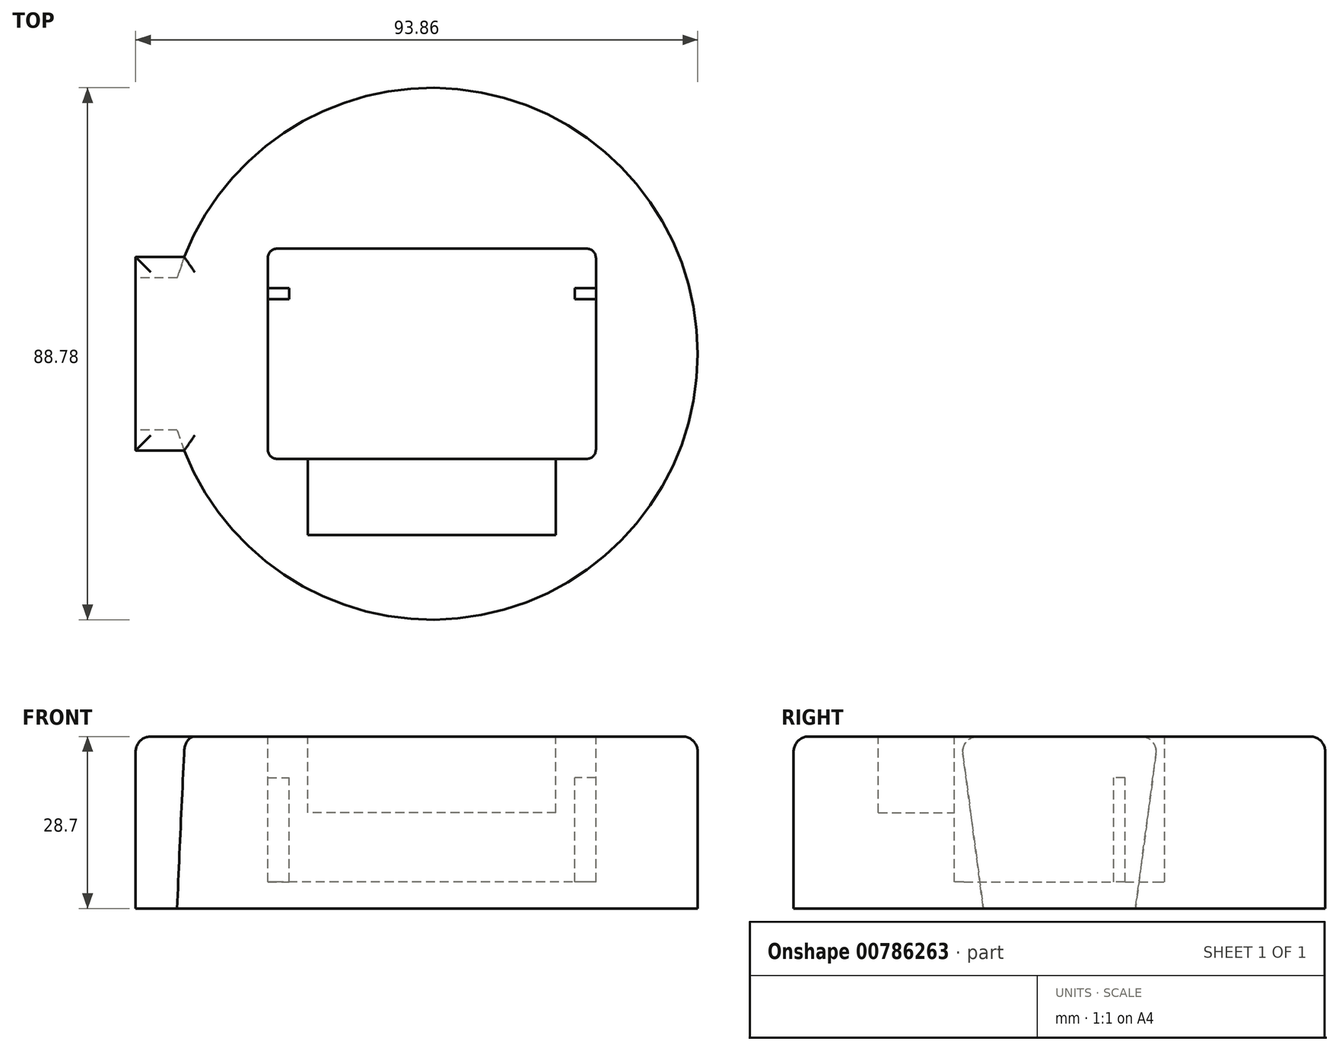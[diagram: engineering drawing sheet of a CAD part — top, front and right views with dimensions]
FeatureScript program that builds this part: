
annotation { "Feature Type Name" : "Feature", "Feature Type Description" : "" }
export const myFeature = defineFeature(function(context is Context, id is Id, definition is map)
    precondition{}
    {
        {
            var Q0;
            Q0=qCreatedBy(makeId("Top.planeOp"),FACE);
            var sketch = newSketch(context, id + "F0", { "sketchPlane" : qUnion([Q0])});
            skCircle(sketch, "E0", {"center": v(0, 0) * mm, "radius": 44.39 * mm});
            skSolve(sketch);
        }
        {
            var Q0;
            Q0 = qSketchRegion(id + "F0", true);
            extrude(context, id + "F1", {"entities" : qUnion([Q0]), "oppositeDirection" : true, "depth" : 28.7 * mm, "offsetDistance" : 25.4 * mm});
        }
        {
            var Q0;
            Q0=makeQuery(id+"F1.opExtrude","CAP_FACE",FACE,{"disambiguationData":[OSD([sQuery(id+"F0.wireOp",EDGE,"E0")])],"isStart":false});
            var sketch = newSketch(context, id + "F2", { "sketchPlane" : qUnion([Q0])});
            skCircle(sketch, "E1", {"center": v(0, 0) * mm, "radius": 35.94 * mm});
            skSolve(sketch);
        }
        {
            var Q0;
            Q0 = qSketchRegion(id + "F2", true);
            extrude(context, id + "F3", {"entities" : qUnion([Q0]), "operationType" : NewBodyOperationType.ADD, "depth" : 21.08 * mm, "offsetDistance" : 25.4 * mm});
        }
        {
            var Q0;
            Q0=makeQuery(id+"F1.opExtrude","CAP_FACE",FACE,{"disambiguationData":[OSD([sQuery(id+"F0.wireOp",EDGE,"E0")])],"isStart":true});
            var sketch = newSketch(context, id + "F4", { "sketchPlane" : qUnion([Q0])});
            skLineSegment(sketch, "E2.bottom", {"start": v(0, 16.51) * mm, "end": v(-49.47, 16.51) * mm});
            skLineSegment(sketch, "E2.top", {"start": v(0, -16.51) * mm, "end": v(-49.47, -16.51) * mm});
            skLineSegment(sketch, "E2.left", {"start": v(0, 16.51) * mm, "end": v(0, -16.51) * mm});
            skLineSegment(sketch, "E2.right", {"start": v(-49.47, 16.5) * mm, "end": v(-49.47, -16.51) * mm});
            skPoint(sketch, "E3", {"position": v(0, 0) * mm});
            skPoint(sketch, "E4.visualSharp", {"position": v(-49.47, 16.51) * mm});
            skPoint(sketch, "E5.visualSharp", {"position": v(-49.47, -16.51) * mm});
            skSolve(sketch);
        }
        {
            var Q0;
            Q0 = qSketchRegion(id + "F4", true);
            var Q1;
            Q1=makeQuery(id+"F1.opExtrude","CAP_FACE",FACE,{"disambiguationData":[OSD([sQuery(id+"F0.wireOp",EDGE,"E0")])],"isStart":false});
            extrude(context, id + "F5", {"entities" : qUnion([Q0]), "operationType" : NewBodyOperationType.ADD, "endBound" : BoundingType.UP_TO_SURFACE, "oppositeDirection" : true, "depth" : 25.4 * mm, "endBoundEntityFace" : qUnion([Q1]), "offsetDistance" : 25.4 * mm});
        }
        {
            var Q0;
            Q0=makeQuery(id+"F5.boolean.opBoolean","MERGE",FACE,{"derivedFrom":[makeQuery(id+"F1.opExtrude","CAP_FACE",FACE,{"disambiguationData":[OSD([sQuery(id+"F0.wireOp",EDGE,"E0")])],"isStart":true}),makeQuery(id+"F5.opExtrude","CAP_FACE",FACE,{"disambiguationData":[OSD([sQuery(id+"F4.wireOp",EDGE,"E2.bottom"),sQuery(id+"F4.wireOp",EDGE,"E2.top"),sQuery(id+"F4.wireOp",EDGE,"E2.left"),sQuery(id+"F4.wireOp",EDGE,"E2.right")])],"isStart":true})]});
            var sketch = newSketch(context, id + "F6", { "sketchPlane" : qUnion([Q0])});
            skLineSegment(sketch, "E6.bottom", {"start": v(25.8, -17.55) * mm, "end": v(-25.8, -17.55) * mm});
            skLineSegment(sketch, "E6.top", {"start": v(25.8, 17.55) * mm, "end": v(-25.8, 17.55) * mm});
            skLineSegment(sketch, "E6.left", {"start": v(27.4, -15.96) * mm, "end": v(27.4, 15.96) * mm});
            skLineSegment(sketch, "E6.right", {"start": v(-27.4, -15.96) * mm, "end": v(-27.4, 15.96) * mm});
            skPoint(sketch, "E6.middle", {"position": v(0, 0) * mm});
            skPoint(sketch, "E7.visualSharp", {"position": v(-27.4, 17.55) * mm});
            skArc(sketch, "E7.filletArc", {"start": v(-25.8, 17.55) * mm, "mid": v(-26.93, 17.09) * mm, "end": v(-27.4, 15.96) * mm});
            skPoint(sketch, "E8.visualSharp", {"position": v(-27.4, -17.55) * mm});
            skArc(sketch, "E8.filletArc", {"start": v(-27.4, -15.96) * mm, "mid": v(-26.93, -17.09) * mm, "end": v(-25.8, -17.55) * mm});
            skPoint(sketch, "E9.visualSharp", {"position": v(27.4, -17.55) * mm});
            skArc(sketch, "E9.filletArc", {"start": v(25.8, -17.55) * mm, "mid": v(26.93, -17.09) * mm, "end": v(27.4, -15.96) * mm});
            skPoint(sketch, "E10.visualSharp", {"position": v(27.4, 17.55) * mm});
            skArc(sketch, "E10.filletArc", {"start": v(27.4, 15.96) * mm, "mid": v(26.93, 17.09) * mm, "end": v(25.8, 17.55) * mm});
            skSolve(sketch);
        }
        {
            var Q0;
            Q0 = qSketchRegion(id + "F6", true);
            extrude(context, id + "F7", {"entities" : qUnion([Q0]), "operationType" : NewBodyOperationType.REMOVE, "oppositeDirection" : true, "depth" : 24.28 * mm, "offsetDistance" : 25.4 * mm});
        }
        {
            var Q0;
            Q0=qCreatedBy(makeId("Top.planeOp"),FACE);
            var sketch = newSketch(context, id + "F8", { "sketchPlane" : qUnion([Q0])});
            skLineSegment(sketch, "E11.bottom", {"start": v(-23.84, 9.1) * mm, "end": v(-27.4, 9.1) * mm});
            skLineSegment(sketch, "E11.top", {"start": v(-23.84, 10.95) * mm, "end": v(-27.4, 10.95) * mm});
            skLineSegment(sketch, "E11.left", {"start": v(-23.84, 9.1) * mm, "end": v(-23.84, 10.95) * mm});
            skLineSegment(sketch, "E11.right", {"start": v(-27.4, 9.1) * mm, "end": v(-27.4, 10.95) * mm});
            skPoint(sketch, "E11.middle", {"position": v(-25.62, 10.02) * mm});
            skLineSegment(sketch, "E12.bottom", {"start": v(23.84, 10.95) * mm, "end": v(27.4, 10.95) * mm});
            skLineSegment(sketch, "E12.top", {"start": v(23.84, 9.1) * mm, "end": v(27.4, 9.1) * mm});
            skLineSegment(sketch, "E12.left", {"start": v(23.84, 10.95) * mm, "end": v(23.84, 9.1) * mm});
            skLineSegment(sketch, "E12.right", {"start": v(27.4, 10.95) * mm, "end": v(27.4, 9.1) * mm});
            skPoint(sketch, "E12.middle", {"position": v(25.62, 10.02) * mm});
            skSolve(sketch);
        }
        {
            var Q0;
            Q0 = qSketchRegion(id + "F8", true);
            var Q1;
            Q1=makeQuery(id+"F7.boolean.opBoolean","COPY",FACE,{"derivedFrom":makeQuery(id+"F7.opExtrude","CAP_FACE",FACE,{"disambiguationData":[OSD([sQuery(id+"F6.wireOp",EDGE,"E6.bottom"),sQuery(id+"F6.wireOp",EDGE,"E6.top"),sQuery(id+"F6.wireOp",EDGE,"E6.left"),sQuery(id+"F6.wireOp",EDGE,"E6.right"),sQuery(id+"F6.wireOp",EDGE,"E7.filletArc"),sQuery(id+"F6.wireOp",EDGE,"E8.filletArc"),sQuery(id+"F6.wireOp",EDGE,"E9.filletArc"),sQuery(id+"F6.wireOp",EDGE,"E10.filletArc")])],"isStart":false})});
            extrude(context, id + "F9", {"entities" : qUnion([Q0]), "operationType" : NewBodyOperationType.ADD, "endBound" : BoundingType.UP_TO_SURFACE, "oppositeDirection" : true, "depth" : 25.4 * mm, "endBoundEntityFace" : qUnion([Q1]), "offsetDistance" : 25.4 * mm});
        }
        {
            var Q0;
            Q0=makeQuery(id+"F9.boolean.opBoolean","MERGE",FACE,{"derivedFrom":[makeQuery(id+"F5.boolean.opBoolean","MERGE",FACE,{"derivedFrom":[makeQuery(id+"F1.opExtrude","CAP_FACE",FACE,{"disambiguationData":[OSD([sQuery(id+"F0.wireOp",EDGE,"E0")])],"isStart":true}),makeQuery(id+"F5.opExtrude","CAP_FACE",FACE,{"disambiguationData":[OSD([sQuery(id+"F4.wireOp",EDGE,"E2.bottom"),sQuery(id+"F4.wireOp",EDGE,"E2.top"),sQuery(id+"F4.wireOp",EDGE,"E2.left"),sQuery(id+"F4.wireOp",EDGE,"E2.right")])],"isStart":true})]}),makeQuery(id+"F9.opExtrude","CAP_FACE",FACE,{"disambiguationData":[OSD([sQuery(id+"F8.wireOp",EDGE,"E11.bottom"),sQuery(id+"F8.wireOp",EDGE,"E11.top"),sQuery(id+"F8.wireOp",EDGE,"E11.left"),sQuery(id+"F8.wireOp",EDGE,"E11.right")])],"isStart":true}),makeQuery(id+"F9.opExtrude","CAP_FACE",FACE,{"disambiguationData":[OSD([sQuery(id+"F8.wireOp",EDGE,"E12.bottom"),sQuery(id+"F8.wireOp",EDGE,"E12.top"),sQuery(id+"F8.wireOp",EDGE,"E12.left"),sQuery(id+"F8.wireOp",EDGE,"E12.right")])],"isStart":true})]});
            var sketch = newSketch(context, id + "F10", { "sketchPlane" : qUnion([Q0])});
            skLineSegment(sketch, "E13.bottom", {"start": v(-27.4, 13.46) * mm, "end": v(27.4, 13.46) * mm});
            skLineSegment(sketch, "E13.top", {"start": v(-27.4, 5.6) * mm, "end": v(27.4, 5.6) * mm});
            skLineSegment(sketch, "E13.left", {"start": v(-27.4, 13.46) * mm, "end": v(-27.4, 5.6) * mm});
            skLineSegment(sketch, "E13.right", {"start": v(27.4, 13.46) * mm, "end": v(27.4, 5.6) * mm});
            skSolve(sketch);
        }
        {
            var Q0;
            Q0 = qSketchRegion(id + "F10", true);
            extrude(context, id + "F11", {"entities" : qUnion([Q0]), "operationType" : NewBodyOperationType.REMOVE, "oppositeDirection" : true, "depth" : 6.86 * mm, "offsetDistance" : 25.4 * mm});
        }
        {
            var Q0;
            Q0=makeQuery(id+"F9.boolean.opBoolean","MERGE",FACE,{"derivedFrom":[makeQuery(id+"F5.boolean.opBoolean","MERGE",FACE,{"derivedFrom":[makeQuery(id+"F1.opExtrude","CAP_FACE",FACE,{"disambiguationData":[OSD([sQuery(id+"F0.wireOp",EDGE,"E0")])],"isStart":true}),makeQuery(id+"F5.opExtrude","CAP_FACE",FACE,{"disambiguationData":[OSD([sQuery(id+"F4.wireOp",EDGE,"E2.bottom"),sQuery(id+"F4.wireOp",EDGE,"E2.top"),sQuery(id+"F4.wireOp",EDGE,"E2.left"),sQuery(id+"F4.wireOp",EDGE,"E2.right")])],"isStart":true})]}),makeQuery(id+"F9.opExtrude","CAP_FACE",FACE,{"disambiguationData":[OSD([sQuery(id+"F8.wireOp",EDGE,"E11.bottom"),sQuery(id+"F8.wireOp",EDGE,"E11.top"),sQuery(id+"F8.wireOp",EDGE,"E11.left"),sQuery(id+"F8.wireOp",EDGE,"E11.right")])],"isStart":true}),makeQuery(id+"F9.opExtrude","CAP_FACE",FACE,{"disambiguationData":[OSD([sQuery(id+"F8.wireOp",EDGE,"E12.bottom"),sQuery(id+"F8.wireOp",EDGE,"E12.top"),sQuery(id+"F8.wireOp",EDGE,"E12.left"),sQuery(id+"F8.wireOp",EDGE,"E12.right")])],"isStart":true})]});
            var sketch = newSketch(context, id + "F12", { "sketchPlane" : qUnion([Q0])});
            skLineSegment(sketch, "E14.bottom", {"start": v(20.7, -30.25) * mm, "end": v(-20.7, -30.25) * mm});
            skLineSegment(sketch, "E14.top", {"start": v(20.7, -17.55) * mm, "end": v(-20.7, -17.55) * mm});
            skLineSegment(sketch, "E14.left", {"start": v(20.7, -30.25) * mm, "end": v(20.7, -17.55) * mm});
            skLineSegment(sketch, "E14.right", {"start": v(-20.7, -30.25) * mm, "end": v(-20.7, -17.55) * mm});
            skPoint(sketch, "E14.middle", {"position": v(0, -23.9) * mm});
            skSolve(sketch);
        }
        {
            var Q0;
            Q0 = qSketchRegion(id + "F12", true);
            extrude(context, id + "F13", {"entities" : qUnion([Q0]), "operationType" : NewBodyOperationType.REMOVE, "oppositeDirection" : true, "depth" : 12.7 * mm, "offsetDistance" : 25.4 * mm});
        }
        {
            var Q0;
            Q0=makeQuery(id+"F5.boolean.opBoolean","MERGE",FACE,{"derivedFrom":[makeQuery(id+"F1.opExtrude","CAP_FACE",FACE,{"disambiguationData":[OSD([sQuery(id+"F0.wireOp",EDGE,"E0")])],"isStart":false}),makeQuery(id+"F5.opExtrude","CAP_FACE",FACE,{"disambiguationData":[OSD([sQuery(id+"F4.wireOp",EDGE,"E2.bottom"),sQuery(id+"F4.wireOp",EDGE,"E2.top"),sQuery(id+"F4.wireOp",EDGE,"E2.left"),sQuery(id+"F4.wireOp",EDGE,"E2.right")])],"isStart":false})]});
            var sketch = newSketch(context, id + "F14", { "sketchPlane" : qUnion([Q0])});
            skCircle(sketch, "E15", {"center": v(0, 0) * mm, "radius": 38.1 * mm});
            skSolve(sketch);
        }
        {
            var Q0;
            Q0 = qSketchRegion(id + "F14", true);
            var Q1;
            Q1=makeQuery(id+"F3.opExtrude","CAP_FACE",FACE,{"disambiguationData":[OSD([sQuery(id+"F2.wireOp",EDGE,"E1")])],"isStart":false});
            extrude(context, id + "F15", {"entities" : qUnion([Q0]), "operationType" : NewBodyOperationType.REMOVE, "endBound" : BoundingType.UP_TO_SURFACE, "depth" : 25.4 * mm, "endBoundEntityFace" : qUnion([Q1]), "offsetDistance" : 25.4 * mm});
        }
        {
            var Q0;
            Q0=makeQuery(id+"F5.opExtrude","SWEPT_FACE",FACE,{"disambiguationData":[OSD([sQuery(id+"F4.wireOp",EDGE,"E2.right")])]});
            var sketch = newSketch(context, id + "F16", { "sketchPlane" : qUnion([Q0])});
            skLineSegment(sketch, "E16", {"start": v(16.51, 0) * mm, "end": v(12.7, -28.7) * mm});
            skLineSegment(sketch, "E17", {"start": v(-12.7, -28.7) * mm, "end": v(-16.51, 0) * mm});
            skLineSegment(sketch, "E18", {"start": v(-16.51, 0) * mm, "end": v(-16.51, -28.7) * mm});
            skLineSegment(sketch, "E19", {"start": v(-16.51, -28.7) * mm, "end": v(-12.7, -28.7) * mm});
            skLineSegment(sketch, "E20", {"start": v(16.51, 0) * mm, "end": v(16.51, -28.7) * mm});
            skLineSegment(sketch, "E21", {"start": v(16.51, -28.7) * mm, "end": v(12.7, -28.7) * mm});
            skSolve(sketch);
        }
        {
            var Q0;
            Q0 = qSketchRegion(id + "F16", true);
            var Q1;
            Q1=makeQuery(id+"F1.opExtrude","SWEPT_FACE",FACE,{"disambiguationData":[OSD([sQuery(id+"F0.wireOp",EDGE,"E0")])]});
            extrude(context, id + "F17", {"entities" : qUnion([Q0]), "operationType" : NewBodyOperationType.REMOVE, "endBound" : BoundingType.UP_TO_SURFACE, "oppositeDirection" : true, "depth" : 25.4 * mm, "endBoundEntityFace" : qUnion([Q1]), "offsetDistance" : 25.4 * mm});
        }
        {
            var Q0;
            Q0=makeQuery(id+"F1.opExtrude","CAP_EDGE",EDGE,{"disambiguationData":[OSD([sQuery(id+"F0.wireOp",EDGE,"E0")])],"isStart":true});
            var Q1;
            Q1=makeQuery(id+"F17.boolean.opBoolean","MERGE",EDGE,{"derivedFrom":[makeQuery(id+"F5.opExtrude","CAP_EDGE",EDGE,{"disambiguationData":[OSD([sQuery(id+"F4.wireOp",EDGE,"E2.top")])],"isStart":true})],"fromTools":[makeQuery(id+"F17.opExtrude","SWEPT_EDGE",EDGE,{"disambiguationData":[OSD([sQuery(id+"F4.wireOp",EDGE,"E2.right"),sQuery(id+"F16.wireOp",EDGE,"E16"),sQuery(id+"F16.wireOp",EDGE,"E20")])]})]});
            var Q2;
            Q2=makeQuery(id+"F17.boolean.opBoolean","COPY",EDGE,{"derivedFrom":makeQuery(id+"F17.opExtrude","CAP_EDGE",EDGE,{"disambiguationData":[OSD([sQuery(id+"F16.wireOp",EDGE,"E16")])],"isStart":true})});
            var Q3;
            Q3=makeQuery(id+"F5.opExtrude","CAP_EDGE",EDGE,{"disambiguationData":[OSD([sQuery(id+"F4.wireOp",EDGE,"E2.right")])],"isStart":true});
            var Q4;
            Q4=makeQuery(id+"F17.boolean.opBoolean","COPY",EDGE,{"derivedFrom":makeQuery(id+"F17.opExtrude","CAP_EDGE",EDGE,{"disambiguationData":[OSD([sQuery(id+"F16.wireOp",EDGE,"E17")])],"isStart":true})});
            var Q5;
            Q5=makeQuery(id+"F17.boolean.opBoolean","MERGE",EDGE,{"derivedFrom":[makeQuery(id+"F5.opExtrude","CAP_EDGE",EDGE,{"disambiguationData":[OSD([sQuery(id+"F4.wireOp",EDGE,"E2.bottom")])],"isStart":true})],"fromTools":[makeQuery(id+"F17.opExtrude","SWEPT_EDGE",EDGE,{"disambiguationData":[OSD([sQuery(id+"F4.wireOp",EDGE,"E2.right"),sQuery(id+"F16.wireOp",EDGE,"E17"),sQuery(id+"F16.wireOp",EDGE,"E18")])]})]});
            var Q6;
            Q6=makeQuery(id+"F17.boolean.opBoolean","COPY",EDGE,{"derivedFrom":makeQuery(id+"F17.opExtrude","SWEPT_EDGE",EDGE,{"disambiguationData":[OSD([sQuery(id+"F4.wireOp",EDGE,"E2.right"),sQuery(id+"F16.wireOp",EDGE,"E16"),sQuery(id+"F16.wireOp",EDGE,"E21")])]})});
            var Q7;
            Q7=makeQuery(id+"F17.boolean.opBoolean","COPY",EDGE,{"derivedFrom":makeQuery(id+"F17.opExtrude","SWEPT_EDGE",EDGE,{"disambiguationData":[OSD([sQuery(id+"F4.wireOp",EDGE,"E2.right"),sQuery(id+"F16.wireOp",EDGE,"E17"),sQuery(id+"F16.wireOp",EDGE,"E19")])]})});
            var Q8;
            Q8=makeQuery(id+"F17.boolean.opBoolean","MERGE",EDGE,{"derivedFrom":[makeQuery(id+"F1.opExtrude","CAP_EDGE",EDGE,{"disambiguationData":[OSD([sQuery(id+"F0.wireOp",EDGE,"E0")])],"isStart":false})],"fromTools":[makeQuery(id+"F17.opExtrude","CAP_EDGE",EDGE,{"disambiguationData":[OSD([sQuery(id+"F16.wireOp",EDGE,"E19")])],"isStart":false}),makeQuery(id+"F17.opExtrude","CAP_EDGE",EDGE,{"disambiguationData":[OSD([sQuery(id+"F16.wireOp",EDGE,"E21")])],"isStart":false})]});
            var Q9;
            Q9=makeQuery(id+"F7.boolean.opBoolean","COPY",EDGE,{"derivedFrom":makeQuery(id+"F7.opExtrude","CAP_EDGE",EDGE,{"disambiguationData":[OSD([sQuery(id+"F6.wireOp",EDGE,"E6.top")])],"isStart":true})});
            var Q10;
            Q10=makeQuery(id+"F13.boolean.opBoolean","COPY",EDGE,{"derivedFrom":makeQuery(id+"F13.opExtrude","CAP_EDGE",EDGE,{"disambiguationData":[OSD([sQuery(id+"F12.wireOp",EDGE,"E14.left")])],"isStart":true})});
            var Q11;
            Q11=makeQuery(id+"F13.boolean.opBoolean","COPY",EDGE,{"derivedFrom":makeQuery(id+"F13.opExtrude","CAP_EDGE",EDGE,{"disambiguationData":[OSD([sQuery(id+"F12.wireOp",EDGE,"E14.bottom")])],"isStart":true})});
            var Q12;
            Q12=makeQuery(id+"F13.boolean.opBoolean","COPY",EDGE,{"derivedFrom":makeQuery(id+"F13.opExtrude","CAP_EDGE",EDGE,{"disambiguationData":[OSD([sQuery(id+"F12.wireOp",EDGE,"E14.right")])],"isStart":true})});
            var Q13;
            Q13=makeQuery(id+"F13.boolean.opBoolean","COPY",EDGE,{"derivedFrom":makeQuery(id+"F13.opExtrude","CAP_EDGE",EDGE,{"disambiguationData":[OSD([sQuery(id+"F12.wireOp",EDGE,"E14.top")])],"isStart":false})});
            var Q14;
            Q14=makeQuery(id+"F13.boolean.opBoolean","COPY",EDGE,{"derivedFrom":makeQuery(id+"F13.opExtrude","SWEPT_EDGE",EDGE,{"disambiguationData":[OSD([sQuery(id+"F6.wireOp",EDGE,"E6.bottom"),sQuery(id+"F12.wireOp",EDGE,"E14.top"),sQuery(id+"F12.wireOp",EDGE,"E14.left")])]})});
            var Q15;
            Q15=makeQuery(id+"F13.boolean.opBoolean","COPY",EDGE,{"derivedFrom":makeQuery(id+"F13.opExtrude","SWEPT_EDGE",EDGE,{"disambiguationData":[OSD([sQuery(id+"F6.wireOp",EDGE,"E6.bottom"),sQuery(id+"F12.wireOp",EDGE,"E14.top"),sQuery(id+"F12.wireOp",EDGE,"E14.right")])]})});
            fillet(context, id + "F18", {"entities" : qUnion([Q0, Q1, Q2, Q3, Q4, Q5, Q6, Q7, Q8, Q9, Q10, Q11, Q12, Q13, Q14, Q15]), "radius" : 2.54 * mm, "tangentPropagation" : true, "allowEdgeOverflow" : false});
        }
    });
